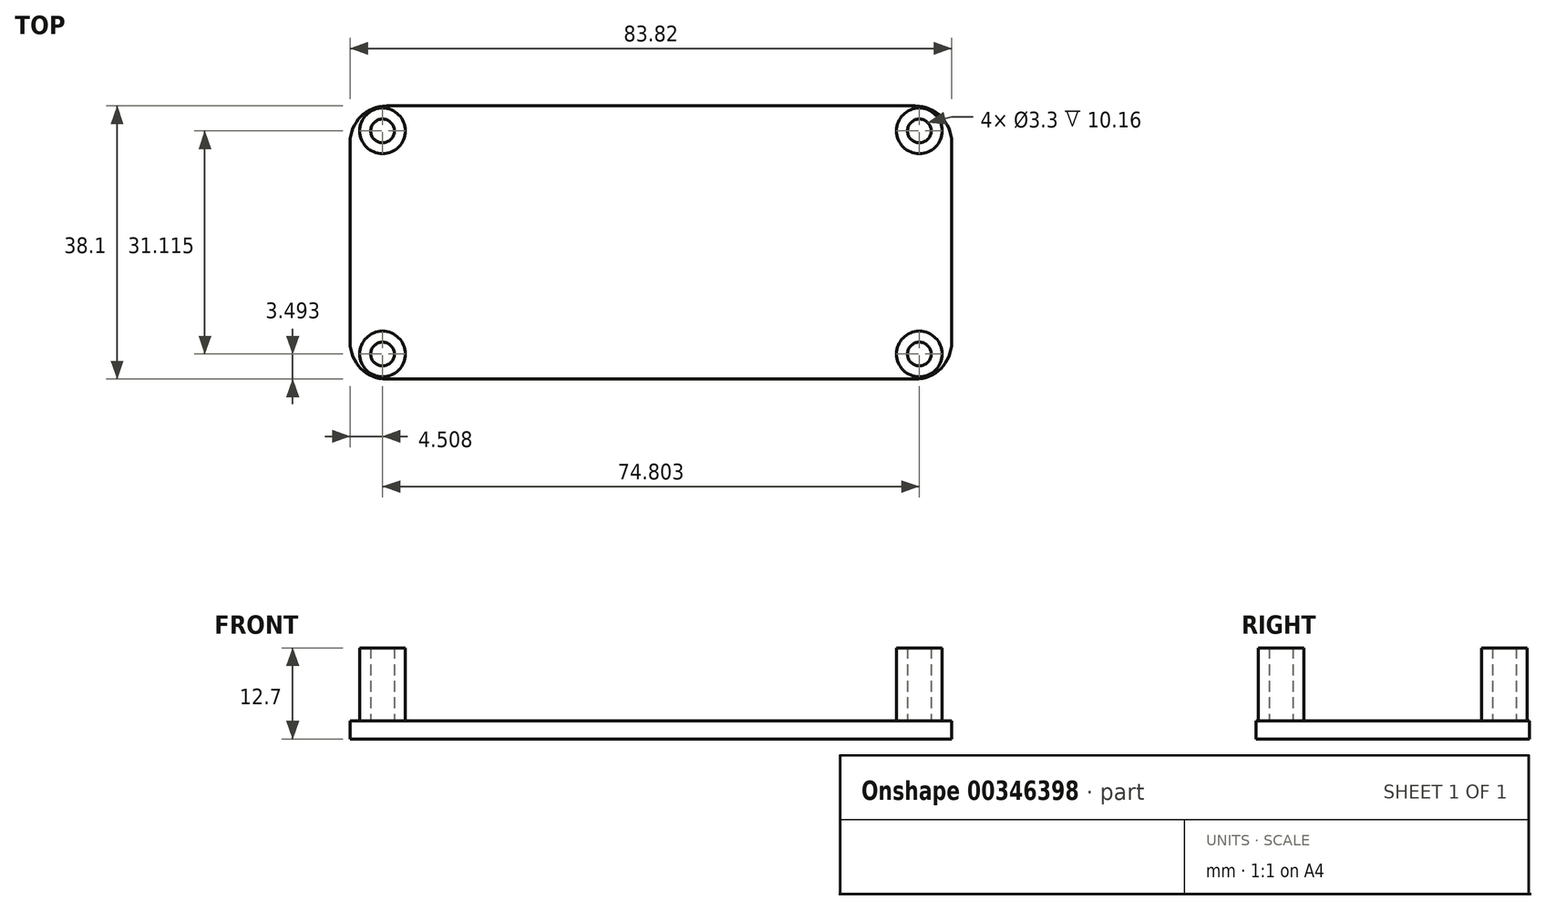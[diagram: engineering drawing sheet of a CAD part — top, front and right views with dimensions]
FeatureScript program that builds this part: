
annotation { "Feature Type Name" : "Feature", "Feature Type Description" : "" }
export const myFeature = defineFeature(function(context is Context, id is Id, definition is map)
    precondition{}
    {
        {
            var Q0;
            Q0=qCreatedBy(makeId("Top.planeOp"),FACE);
            var sketch = newSketch(context, id + "F0", { "sketchPlane" : qUnion([Q0])});
            skLineSegment(sketch, "E0.bottom", {"start": v(41.91, -19.05) * mm, "end": v(-41.91, -19.05) * mm});
            skLineSegment(sketch, "E0.top", {"start": v(41.91, 19.05) * mm, "end": v(-41.91, 19.05) * mm});
            skLineSegment(sketch, "E0.left", {"start": v(41.91, -19.05) * mm, "end": v(41.91, 19.05) * mm});
            skLineSegment(sketch, "E0.right", {"start": v(-41.91, -19.05) * mm, "end": v(-41.91, 19.05) * mm});
            skPoint(sketch, "E0.middle", {"position": v(0, 0) * mm});
            skLineSegment(sketch, "E1.bottom", {"start": v(-37.4, -15.56) * mm, "end": v(37.4, -15.56) * mm});
            skLineSegment(sketch, "E1.top", {"start": v(-37.4, 15.56) * mm, "end": v(37.4, 15.56) * mm});
            skLineSegment(sketch, "E1.left", {"start": v(-37.4, -15.56) * mm, "end": v(-37.4, 15.56) * mm});
            skLineSegment(sketch, "E1.right", {"start": v(37.4, -15.56) * mm, "end": v(37.4, 15.56) * mm});
            skSolve(sketch);
        }
        {
            var Q0;
            Q0=qCreatedBy(makeId("Top.planeOp"),FACE);
            var sketch = newSketch(context, id + "F1", { "sketchPlane" : qUnion([Q0])});
            skLineSegment(sketch, "E2.0", {"start": v(41.91, -19.05) * mm, "end": v(-41.91, -19.05) * mm});
            skLineSegment(sketch, "E3.0", {"start": v(-41.91, -19.05) * mm, "end": v(-41.91, 19.05) * mm});
            skLineSegment(sketch, "E4.0", {"start": v(41.91, 19.05) * mm, "end": v(-41.91, 19.05) * mm});
            skLineSegment(sketch, "E5.0", {"start": v(41.91, -19.05) * mm, "end": v(41.91, 19.05) * mm});
            skPoint(sketch, "E6.0", {"position": v(-37.4, -15.56) * mm});
            skPoint(sketch, "E7.0", {"position": v(-37.4, 15.56) * mm});
            skPoint(sketch, "E8.0", {"position": v(37.4, -15.56) * mm});
            skPoint(sketch, "E9.0", {"position": v(37.4, 15.56) * mm});
            skCircle(sketch, "E10", {"center": v(-37.4, -15.56) * mm, "radius": 1.65 * mm});
            skCircle(sketch, "E11", {"center": v(-37.4, 15.56) * mm, "radius": 1.65 * mm});
            skCircle(sketch, "E12", {"center": v(37.4, -15.56) * mm, "radius": 1.65 * mm});
            skCircle(sketch, "E13", {"center": v(37.4, 15.56) * mm, "radius": 1.65 * mm});
            skCircle(sketch, "E14", {"center": v(-37.4, 15.56) * mm, "radius": 3.18 * mm});
            skCircle(sketch, "E15", {"center": v(-37.4, -15.56) * mm, "radius": 3.18 * mm});
            skCircle(sketch, "E16", {"center": v(37.4, -15.56) * mm, "radius": 3.18 * mm});
            skCircle(sketch, "E17", {"center": v(37.4, 15.56) * mm, "radius": 3.18 * mm});
            skSolve(sketch);
        }
        {
            var Q0;
            Q0=makeQuery(id+"F1.imprint","IMPRINT",FACE,{"disambiguationData":[TD([[makeQuery(id+"F1.imprint","IMPRINT",EDGE,{"derivedFrom":sQuery(id+"F1.wireOp",EDGE,"E11")}),-1.0]])]});
            var Q1;
            Q1=makeQuery(id+"F1.imprint","IMPRINT",FACE,{"disambiguationData":[TD([[makeQuery(id+"F1.imprint","IMPRINT",EDGE,{"derivedFrom":sQuery(id+"F1.wireOp",EDGE,"E2.0")}),-1.0]])]});
            var Q2;
            Q2=makeQuery(id+"F1.imprint","IMPRINT",FACE,{"disambiguationData":[TD([[makeQuery(id+"F1.imprint","IMPRINT",EDGE,{"derivedFrom":sQuery(id+"F1.wireOp",EDGE,"E13")}),1.0]])]});
            var Q3;
            Q3=makeQuery(id+"F1.imprint","IMPRINT",FACE,{"disambiguationData":[TD([[makeQuery(id+"F1.imprint","IMPRINT",EDGE,{"derivedFrom":sQuery(id+"F1.wireOp",EDGE,"E11")}),1.0]])]});
            var Q4;
            Q4=makeQuery(id+"F1.imprint","IMPRINT",FACE,{"disambiguationData":[TD([[makeQuery(id+"F1.imprint","IMPRINT",EDGE,{"derivedFrom":sQuery(id+"F1.wireOp",EDGE,"E12")}),-1.0]])]});
            var Q5;
            Q5=makeQuery(id+"F1.imprint","IMPRINT",FACE,{"disambiguationData":[TD([[makeQuery(id+"F1.imprint","IMPRINT",EDGE,{"derivedFrom":sQuery(id+"F1.wireOp",EDGE,"E10")}),1.0]])]});
            var Q6;
            Q6=makeQuery(id+"F1.imprint","IMPRINT",FACE,{"disambiguationData":[TD([[makeQuery(id+"F1.imprint","IMPRINT",EDGE,{"derivedFrom":sQuery(id+"F1.wireOp",EDGE,"E13")}),-1.0]])]});
            var Q7;
            Q7=makeQuery(id+"F1.imprint","IMPRINT",FACE,{"disambiguationData":[TD([[makeQuery(id+"F1.imprint","IMPRINT",EDGE,{"derivedFrom":sQuery(id+"F1.wireOp",EDGE,"E12")}),1.0]])]});
            var Q8;
            Q8=makeQuery(id+"F1.imprint","IMPRINT",FACE,{"disambiguationData":[TD([[makeQuery(id+"F1.imprint","IMPRINT",EDGE,{"derivedFrom":sQuery(id+"F1.wireOp",EDGE,"E10")}),-1.0]])]});
            extrude(context, id + "F2", {"entities" : qUnion([Q0, Q1, Q2, Q3, Q4, Q5, Q6, Q7, Q8]), "oppositeDirection" : true, "depth" : 2.54 * mm, "offsetDistance" : 25 * mm});
        }
        {
            var Q0;
            Q0=makeQuery(id+"F1.imprint","IMPRINT",FACE,{"disambiguationData":[TD([[makeQuery(id+"F1.imprint","IMPRINT",EDGE,{"derivedFrom":sQuery(id+"F1.wireOp",EDGE,"E10")}),-1.0]])]});
            var Q1;
            Q1=makeQuery(id+"F1.imprint","IMPRINT",FACE,{"disambiguationData":[TD([[makeQuery(id+"F1.imprint","IMPRINT",EDGE,{"derivedFrom":sQuery(id+"F1.wireOp",EDGE,"E11")}),-1.0]])]});
            var Q2;
            Q2=makeQuery(id+"F1.imprint","IMPRINT",FACE,{"disambiguationData":[TD([[makeQuery(id+"F1.imprint","IMPRINT",EDGE,{"derivedFrom":sQuery(id+"F1.wireOp",EDGE,"E12")}),-1.0]])]});
            var Q3;
            Q3=makeQuery(id+"F1.imprint","IMPRINT",FACE,{"disambiguationData":[TD([[makeQuery(id+"F1.imprint","IMPRINT",EDGE,{"derivedFrom":sQuery(id+"F1.wireOp",EDGE,"E13")}),-1.0]])]});
            extrude(context, id + "F3", {"entities" : qUnion([Q0, Q1, Q2, Q3]), "operationType" : NewBodyOperationType.ADD, "depth" : 10.16 * mm, "offsetDistance" : 25 * mm});
        }
        {
            var Q0;
            Q0=makeQuery(id+"F2.opExtrude","SWEPT_EDGE",EDGE,{"disambiguationData":[OSD([sQuery(id+"F1.wireOp",EDGE,"E2.0"),sQuery(id+"F1.wireOp",EDGE,"E3.0")])]});
            var Q1;
            Q1=makeQuery(id+"F2.opExtrude","SWEPT_EDGE",EDGE,{"disambiguationData":[OSD([sQuery(id+"F1.wireOp",EDGE,"E2.0"),sQuery(id+"F1.wireOp",EDGE,"E5.0")])]});
            var Q2;
            Q2=makeQuery(id+"F2.opExtrude","SWEPT_EDGE",EDGE,{"disambiguationData":[OSD([sQuery(id+"F1.wireOp",EDGE,"E4.0"),sQuery(id+"F1.wireOp",EDGE,"E5.0")])]});
            var Q3;
            Q3=makeQuery(id+"F2.opExtrude","SWEPT_EDGE",EDGE,{"disambiguationData":[OSD([sQuery(id+"F1.wireOp",EDGE,"E3.0"),sQuery(id+"F1.wireOp",EDGE,"E4.0")])]});
            fillet(context, id + "F4", {"entities" : qUnion([Q0, Q1, Q2, Q3]), "radius" : 5.08 * mm, "tangentPropagation" : true, "allowEdgeOverflow" : false});
        }
    });
